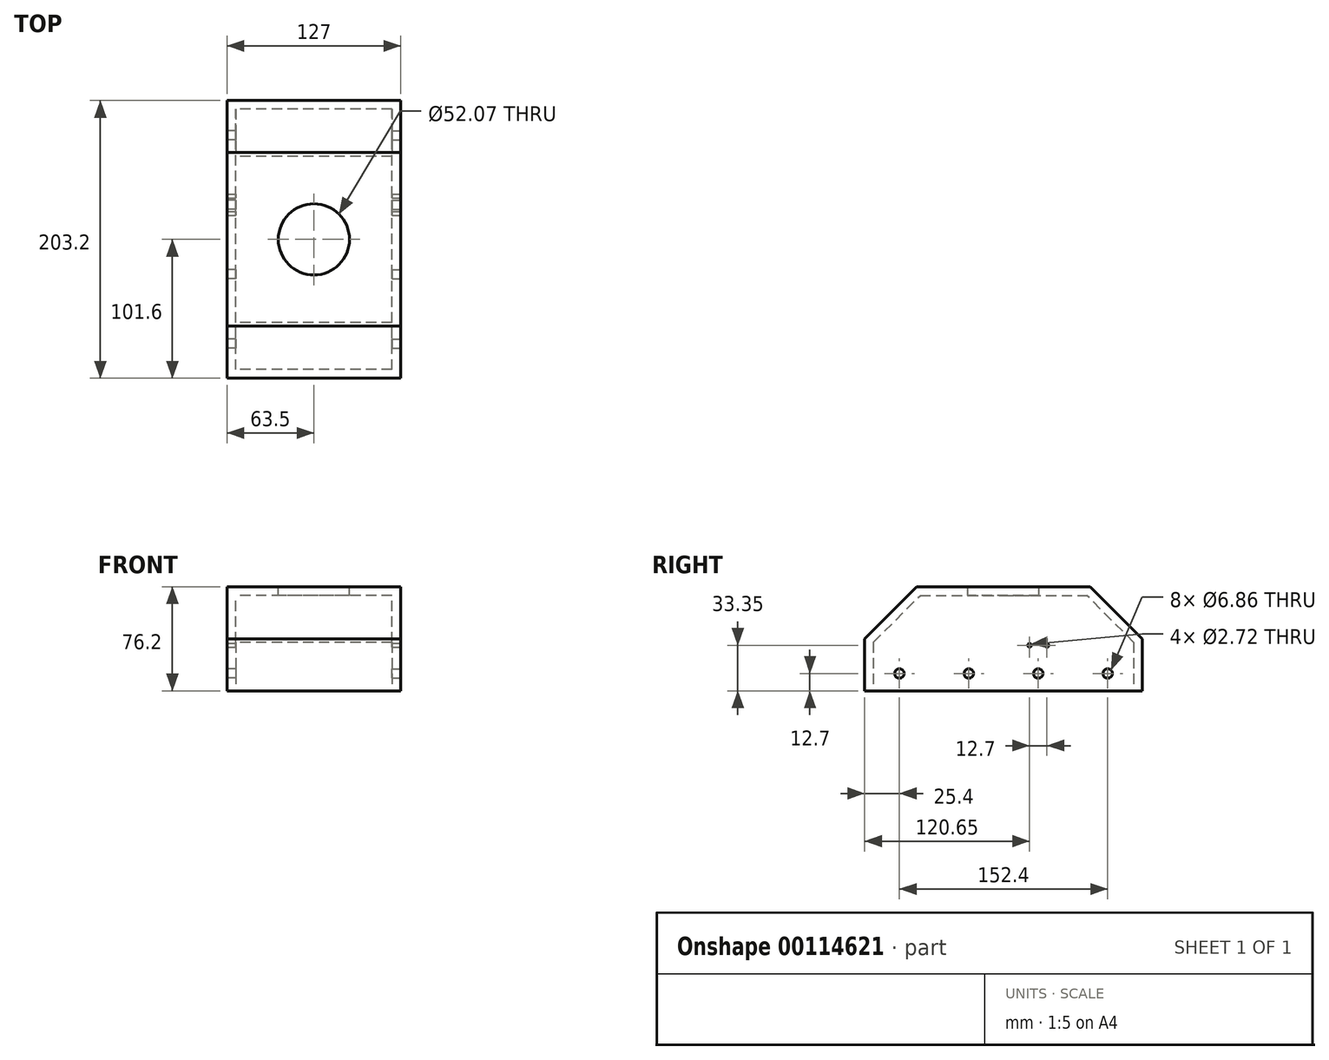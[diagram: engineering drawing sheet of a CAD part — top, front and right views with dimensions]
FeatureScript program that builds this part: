
annotation { "Feature Type Name" : "Feature", "Feature Type Description" : "" }
export const myFeature = defineFeature(function(context is Context, id is Id, definition is map)
    precondition{}
    {
        {
            var Q0;
            Q0=qCreatedBy(makeId("Front.planeOp"),FACE);
            var sketch = newSketch(context, id + "F0", { "sketchPlane" : qUnion([Q0])});
            skLineSegment(sketch, "E0.bottom", {"start": v(63.5, -38.1) * mm, "end": v(-63.5, -38.1) * mm, "construction": true});
            skLineSegment(sketch, "E0.top", {"start": v(63.5, 38.1) * mm, "end": v(-63.5, 38.1) * mm, "construction": true});
            skLineSegment(sketch, "E0.left", {"start": v(63.5, -38.1) * mm, "end": v(63.5, 38.1) * mm, "construction": true});
            skLineSegment(sketch, "E0.right", {"start": v(-63.5, -38.1) * mm, "end": v(-63.5, 38.1) * mm, "construction": true});
            skPoint(sketch, "E0.middle", {"position": v(0, 0) * mm});
            skLineSegment(sketch, "E1.bottom", {"start": v(57.15, -31.75) * mm, "end": v(-57.15, -31.75) * mm, "construction": true});
            skLineSegment(sketch, "E1.top", {"start": v(57.15, 31.75) * mm, "end": v(-57.15, 31.75) * mm, "construction": true});
            skLineSegment(sketch, "E1.left", {"start": v(57.15, -31.75) * mm, "end": v(57.15, 31.75) * mm, "construction": true});
            skLineSegment(sketch, "E1.right", {"start": v(-57.15, -31.75) * mm, "end": v(-57.15, 31.75) * mm, "construction": true});
            skLineSegment(sketch, "E2", {"start": v(-57.15, 31.75) * mm, "end": v(-57.15, -38.1) * mm});
            skLineSegment(sketch, "E3", {"start": v(-57.15, -38.1) * mm, "end": v(-63.5, -38.1) * mm});
            skLineSegment(sketch, "E4", {"start": v(-63.5, 38.1) * mm, "end": v(-63.5, -38.1) * mm});
            skLineSegment(sketch, "E5", {"start": v(-63.5, 38.1) * mm, "end": v(63.5, 38.1) * mm});
            skLineSegment(sketch, "E6", {"start": v(63.5, 38.1) * mm, "end": v(63.5, -38.1) * mm});
            skLineSegment(sketch, "E7", {"start": v(-57.15, 31.75) * mm, "end": v(57.15, 31.75) * mm});
            skLineSegment(sketch, "E8", {"start": v(57.15, 31.75) * mm, "end": v(57.15, -38.1) * mm});
            skLineSegment(sketch, "E9", {"start": v(57.15, -38.1) * mm, "end": v(63.5, -38.1) * mm});
            skSolve(sketch);
        }
        {
            var Q0;
            Q0 = qSketchRegion(id + "F0", true);
            extrude(context, id + "F1", {"entities" : qUnion([Q0]), "endBound" : BoundingType.SYMMETRIC, "depth" : 203.2 * mm});
        }
        {
            var Q0;
            Q0=makeQuery(id+"F1.opExtrude","SWEPT_FACE",FACE,{"disambiguationData":[OSD([sQuery(id+"F0.wireOp",EDGE,"E6")])]});
            var sketch = newSketch(context, id + "F2", { "sketchPlane" : qUnion([Q0])});
            skLineSegment(sketch, "E10", {"start": v(-101.6, -38.1) * mm, "end": v(-101.6, -25.4) * mm, "construction": true});
            skLineSegment(sketch, "E11", {"start": v(-101.6, -25.4) * mm, "end": v(-76.2, -25.4) * mm, "construction": true});
            skLineSegment(sketch, "E12", {"start": v(-76.2, -25.4) * mm, "end": v(-25.4, -25.4) * mm, "construction": true});
            skLineSegment(sketch, "E13", {"start": v(-25.4, -25.4) * mm, "end": v(25.4, -25.4) * mm, "construction": true});
            skLineSegment(sketch, "E14", {"start": v(25.4, -25.4) * mm, "end": v(76.2, -25.4) * mm, "construction": true});
            skLineSegment(sketch, "E15", {"start": v(76.2, -25.4) * mm, "end": v(101.6, -25.4) * mm, "construction": true});
            skCircle(sketch, "E16", {"center": v(-76.2, -25.4) * mm, "radius": 3.43 * mm});
            skCircle(sketch, "E17", {"center": v(-25.4, -25.4) * mm, "radius": 3.43 * mm});
            skCircle(sketch, "E18", {"center": v(25.4, -25.4) * mm, "radius": 3.43 * mm});
            skCircle(sketch, "E19", {"center": v(76.2, -25.4) * mm, "radius": 3.43 * mm});
            skSolve(sketch);
        }
        {
            var Q0;
            Q0=makeQuery(id+"F1.opExtrude","SWEPT_FACE",FACE,{"disambiguationData":[OSD([sQuery(id+"F0.wireOp",EDGE,"E4")])]});
            var sketch = newSketch(context, id + "F3", { "sketchPlane" : qUnion([Q0])});
            skCircle(sketch, "E20.0", {"center": v(-76.2, -25.4) * mm, "radius": 3.43 * mm});
            skCircle(sketch, "E21.0", {"center": v(-25.4, -25.4) * mm, "radius": 3.43 * mm});
            skCircle(sketch, "E22.0", {"center": v(25.4, -25.4) * mm, "radius": 3.43 * mm});
            skCircle(sketch, "E23.0", {"center": v(76.2, -25.4) * mm, "radius": 3.43 * mm});
            skSolve(sketch);
        }
        {
            var Q0;
            Q0 = qSketchRegion(id + "F3", true);
            extrude(context, id + "F4", {"entities" : qUnion([Q0]), "operationType" : NewBodyOperationType.REMOVE, "oppositeDirection" : true, "depth" : 6.35 * mm});
        }
        {
            var Q0;
            Q0 = qSketchRegion(id + "F2", true);
            extrude(context, id + "F5", {"entities" : qUnion([Q0]), "operationType" : NewBodyOperationType.REMOVE, "oppositeDirection" : true, "depth" : 6.35 * mm});
        }
        {
            var Q0;
            Q0=makeQuery(id+"F1.opExtrude","SWEPT_FACE",FACE,{"disambiguationData":[OSD([sQuery(id+"F0.wireOp",EDGE,"E5")])]});
            var sketch = newSketch(context, id + "F6", { "sketchPlane" : qUnion([Q0])});
            skCircle(sketch, "E24", {"center": v(0, 0) * mm, "radius": 26.04 * mm});
            skSolve(sketch);
        }
        {
            var Q0;
            Q0 = qSketchRegion(id + "F6", true);
            extrude(context, id + "F7", {"entities" : qUnion([Q0]), "operationType" : NewBodyOperationType.REMOVE, "oppositeDirection" : true, "depth" : 6.35 * mm});
        }
        {
            var Q0;
            Q0=makeQuery(id+"F1.opExtrude","SWEPT_FACE",FACE,{"disambiguationData":[OSD([sQuery(id+"F0.wireOp",EDGE,"E6")])]});
            var sketch = newSketch(context, id + "F8", { "sketchPlane" : qUnion([Q0])});
            skLineSegment(sketch, "E25", {"start": v(101.6, -38.1) * mm, "end": v(101.6, -4.75) * mm, "construction": true});
            skLineSegment(sketch, "E26", {"start": v(101.6, -4.75) * mm, "end": v(31.75, -4.75) * mm, "construction": true});
            skLineSegment(sketch, "E27", {"start": v(31.75, -4.75) * mm, "end": v(19.05, -4.75) * mm, "construction": true});
            skCircle(sketch, "E28", {"center": v(19.05, -4.75) * mm, "radius": 1.36 * mm});
            skCircle(sketch, "E29", {"center": v(31.75, -4.75) * mm, "radius": 1.36 * mm});
            skSolve(sketch);
        }
        {
            var Q0;
            Q0 = qSketchRegion(id + "F8", true);
            extrude(context, id + "F9", {"entities" : qUnion([Q0]), "operationType" : NewBodyOperationType.REMOVE, "endBound" : BoundingType.THROUGH_ALL, "oppositeDirection" : true, "depth" : 25.4 * mm, "offsetDistance" : 25.4 * mm});
        }
        {
            var Q0;
            Q0=makeQuery(id+"F1.opExtrude","SWEPT_FACE",FACE,{"disambiguationData":[OSD([sQuery(id+"F0.wireOp",EDGE,"E6")])]});
            var sketch = newSketch(context, id + "F10", { "sketchPlane" : qUnion([Q0])});
            skLineSegment(sketch, "E30", {"start": v(-101.6, 38.1) * mm, "end": v(-101.6, 0) * mm});
            skLineSegment(sketch, "E31", {"start": v(-101.6, 0) * mm, "end": v(-63.5, 38.1) * mm});
            skLineSegment(sketch, "E32", {"start": v(-63.5, 38.1) * mm, "end": v(-101.6, 38.1) * mm});
            skLineSegment(sketch, "E33", {"start": v(0, 0) * mm, "end": v(0, -38.1) * mm, "construction": true});
            skLineSegment(sketch, "E34.MirrorCS", {"start": v(101.6, 0) * mm, "end": v(63.5, 38.1) * mm});
            skLineSegment(sketch, "E35.MirrorCS", {"start": v(63.5, 38.1) * mm, "end": v(101.6, 38.1) * mm});
            skLineSegment(sketch, "E36.MirrorCS", {"start": v(101.6, 38.1) * mm, "end": v(101.6, 0) * mm});
            skSolve(sketch);
        }
        {
            var Q0;
            Q0 = qSketchRegion(id + "F10", true);
            extrude(context, id + "F11", {"entities" : qUnion([Q0]), "operationType" : NewBodyOperationType.REMOVE, "endBound" : BoundingType.THROUGH_ALL, "oppositeDirection" : true, "depth" : 25.4 * mm, "offsetDistance" : 25.4 * mm});
        }
        {
            var Q0;
            Q0=makeQuery(id+"F1.opExtrude","SWEPT_FACE",FACE,{"disambiguationData":[OSD([sQuery(id+"F0.wireOp",EDGE,"E2")])]});
            var sketch = newSketch(context, id + "F12", { "sketchPlane" : qUnion([Q0])});
            skLineSegment(sketch, "E37.0", {"start": v(-101.6, 0) * mm, "end": v(-101.6, -38.1) * mm});
            skLineSegment(sketch, "E38.0", {"start": v(-101.6, 0) * mm, "end": v(-69.85, 31.75) * mm});
            skLineSegment(sketch, "E39.0", {"start": v(-95.25, -2.63) * mm, "end": v(-60.87, 31.75) * mm});
            skLineSegment(sketch, "E39.1", {"start": v(-95.25, -2.63) * mm, "end": v(-95.25, -38.1) * mm});
            skLineSegment(sketch, "E40", {"start": v(-60.87, 31.75) * mm, "end": v(-60.87, 31.75) * mm});
            skLineSegment(sketch, "E41.0", {"start": v(-101.6, -38.1) * mm, "end": v(101.6, -38.1) * mm});
            skLineSegment(sketch, "E42", {"start": v(-69.85, 31.75) * mm, "end": v(-60.87, 31.75) * mm});
            skLineSegment(sketch, "E43", {"start": v(0, -38.1) * mm, "end": v(0, -24.57) * mm, "construction": true});
            skLineSegment(sketch, "E44.MirrorCS", {"start": v(95.25, -2.63) * mm, "end": v(60.87, 31.75) * mm});
            skLineSegment(sketch, "E45.MirrorCS", {"start": v(95.25, -2.63) * mm, "end": v(95.25, -38.1) * mm});
            skLineSegment(sketch, "E46.MirrorCS", {"start": v(101.6, 0) * mm, "end": v(69.85, 31.75) * mm});
            skLineSegment(sketch, "E47.MirrorCS", {"start": v(101.6, 0) * mm, "end": v(101.6, -38.1) * mm});
            skLineSegment(sketch, "E48.MirrorCS", {"start": v(69.85, 31.75) * mm, "end": v(60.87, 31.75) * mm});
            skSolve(sketch);
        }
        {
            var Q0;
            Q0 = qSketchRegion(id + "F12", true);
            extrude(context, id + "F13", {"entities" : qUnion([Q0]), "operationType" : NewBodyOperationType.ADD, "endBound" : BoundingType.UP_TO_NEXT, "depth" : 25.4 * mm, "offsetDistance" : 25.4 * mm});
        }
    });
